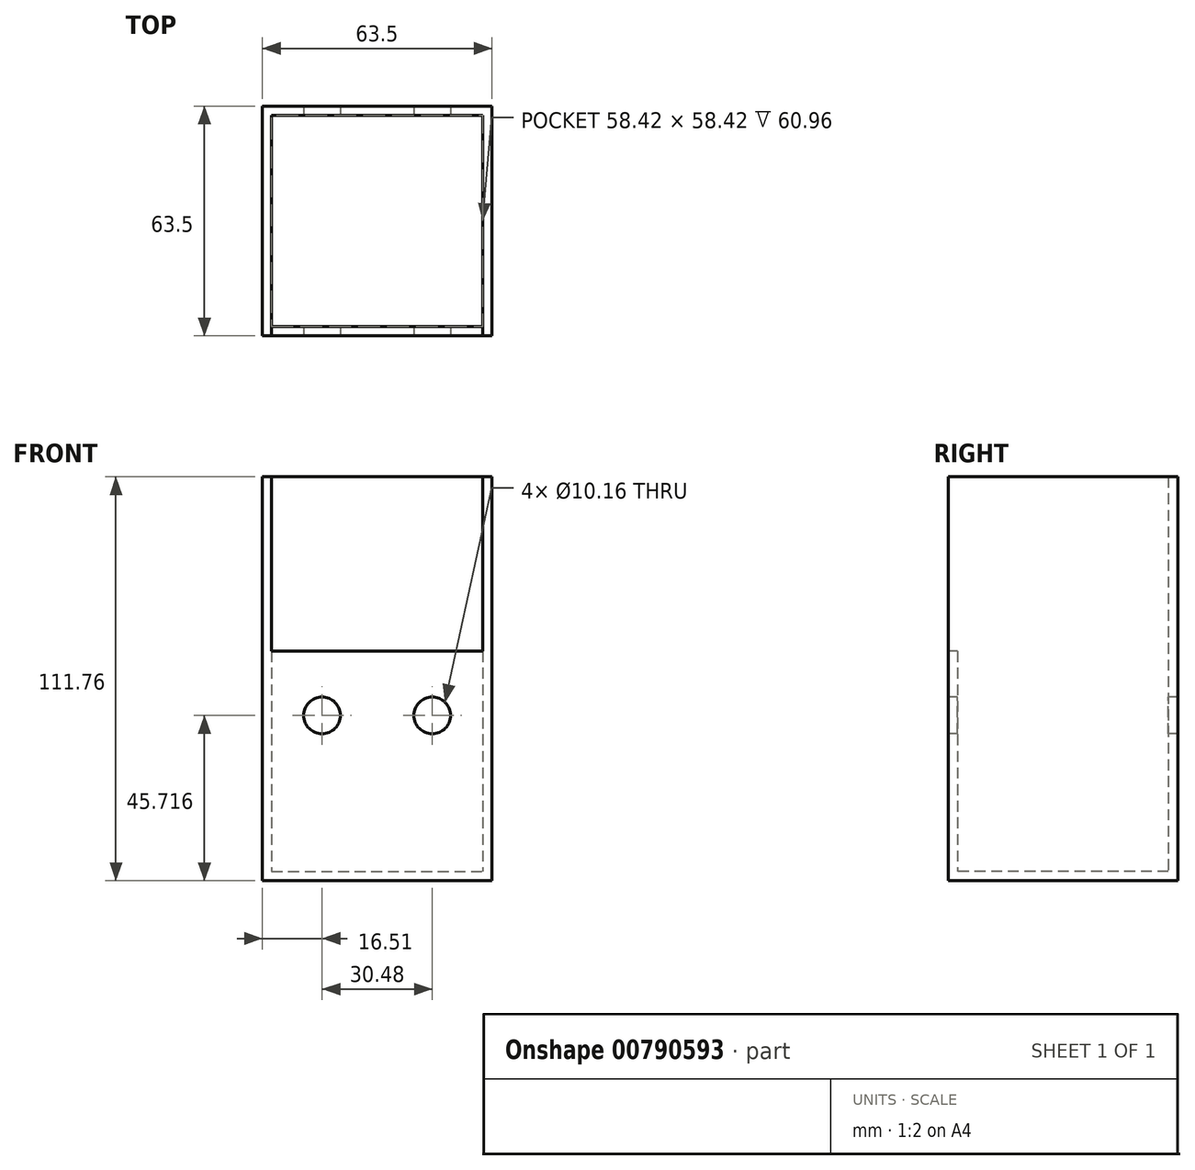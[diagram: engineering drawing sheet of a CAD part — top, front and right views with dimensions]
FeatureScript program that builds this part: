
annotation { "Feature Type Name" : "Feature", "Feature Type Description" : "" }
export const myFeature = defineFeature(function(context is Context, id is Id, definition is map)
    precondition{}
    {
        {
            var Q0;
            Q0=qCreatedBy(makeId("Front.planeOp"),FACE);
            var sketch = newSketch(context, id + "F0", { "sketchPlane" : qUnion([Q0])});
            skLineSegment(sketch, "E0.bottom", {"start": v(-31.75, 31.43) * mm, "end": v(31.75, 31.43) * mm});
            skLineSegment(sketch, "E0.top", {"start": v(-31.75, -80.33) * mm, "end": v(31.75, -80.33) * mm});
            skLineSegment(sketch, "E0.left", {"start": v(-31.75, 31.43) * mm, "end": v(-31.75, -80.33) * mm});
            skLineSegment(sketch, "E0.right", {"start": v(31.75, 31.43) * mm, "end": v(31.75, -80.33) * mm});
            skLineSegment(sketch, "E1", {"start": v(0, 61) * mm, "end": v(0, -102.2) * mm, "construction": true});
            skSolve(sketch);
        }
        {
            var Q0;
            Q0 = qSketchRegion(id + "F0", true);
            extrude(context, id + "F1", {"entities" : qUnion([Q0]), "oppositeDirection" : true, "depth" : 63.5 * mm, "offsetDistance" : 25.4 * mm});
        }
        {
            var Q0;
            Q0=makeQuery(id+"F1.opExtrude","CAP_FACE",FACE,{"disambiguationData":[OSD([sQuery(id+"F0.wireOp",EDGE,"E0.bottom"),sQuery(id+"F0.wireOp",EDGE,"E0.top"),sQuery(id+"F0.wireOp",EDGE,"E0.left"),sQuery(id+"F0.wireOp",EDGE,"E0.right")])],"isStart":true});
            var sketch = newSketch(context, id + "F2", { "sketchPlane" : qUnion([Q0])});
            skLineSegment(sketch, "E2.bottom", {"start": v(-29.21, 31.43) * mm, "end": v(29.21, 31.43) * mm});
            skLineSegment(sketch, "E2.top", {"start": v(-29.21, -16.83) * mm, "end": v(29.21, -16.83) * mm});
            skLineSegment(sketch, "E2.left", {"start": v(-29.21, 31.43) * mm, "end": v(-29.21, -16.83) * mm});
            skLineSegment(sketch, "E2.right", {"start": v(29.21, 31.43) * mm, "end": v(29.21, -16.83) * mm});
            skSolve(sketch);
        }
        {
            var Q0;
            Q0=makeQuery(id+"F1.opExtrude","SWEPT_FACE",FACE,{"disambiguationData":[OSD([sQuery(id+"F0.wireOp",EDGE,"E0.bottom")])]});
            shell(context, id + "F3", {"entities" : qUnion([Q0]), "thickness" : 2.54 * mm});
        }
        {
            var Q0;
            Q0=makeQuery(id+"F2.imprint","IMPRINT",FACE,{"disambiguationData":[TD([[makeQuery(id+"F2.imprint","IMPRINT",EDGE,{"derivedFrom":sQuery(id+"F2.wireOp",EDGE,"E2.bottom")}),-1.0]])]});
            extrude(context, id + "F4", {"entities" : qUnion([Q0]), "operationType" : NewBodyOperationType.REMOVE, "oppositeDirection" : true, "depth" : 25.4 * mm, "offsetDistance" : 25.4 * mm});
        }
        {
            var Q0;
            Q0=makeQuery(id+"F1.opExtrude","CAP_FACE",FACE,{"disambiguationData":[OSD([sQuery(id+"F0.wireOp",EDGE,"E0.bottom"),sQuery(id+"F0.wireOp",EDGE,"E0.top"),sQuery(id+"F0.wireOp",EDGE,"E0.left"),sQuery(id+"F0.wireOp",EDGE,"E0.right")])],"isStart":true});
            var sketch = newSketch(context, id + "F5", { "sketchPlane" : qUnion([Q0])});
            skCircle(sketch, "E3", {"center": v(-15.24, -34.61) * mm, "radius": 5.08 * mm});
            skCircle(sketch, "E4", {"center": v(15.24, -34.61) * mm, "radius": 5.08 * mm});
            skSolve(sketch);
        }
        {
            var Q0;
            Q0 = qSketchRegion(id + "F5", true);
            extrude(context, id + "F6", {"entities" : qUnion([Q0]), "operationType" : NewBodyOperationType.REMOVE, "oppositeDirection" : true, "depth" : 254 * mm, "offsetDistance" : 25.4 * mm});
        }
    });
